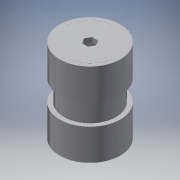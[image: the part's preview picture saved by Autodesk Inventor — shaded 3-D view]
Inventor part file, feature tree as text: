
AUTODESK INVENTOR PART (.ipt)
format: ipt  version: 2016 (Build 200138000, 138)  size: 152,064 bytes
history: native  units: in
note: dims shown in document units (in); Inventor stores cm internally (conversion verified against a paired STEP export)
features: extrude x6, sketch x6
ambient origin geometry x8: Origin, YZ Plane, XZ Plane, XY Plane, X Axis, Y Axis, Z Axis, Center Point
bodies: Body1 (feature_tree)
feature tree (12):
  extrude  "Extrusion5"  Depth=0.203in
  extrude  "Extrusion6"  Depth=2.5in
  extrude  "Extrusion7"  Depth=1.5in TaperAngle=0.0deg
  extrude  "Extrusion8"  Depth=1.5in TaperAngle=0.0deg
  extrude  "Extrusion9"  Depth=0.203in TaperAngle=0.0deg
  extrude  "Extrusion10"  Depth=0.5in TaperAngle=0.0deg
  sketch  "Sketch6"  dims[d16=2.5in d17=0.203in]
  sketch  "Sketch7"  dims[d18=2.5in d19=0.0in d20=2.5in]
  sketch  "Sketch8"  dims[d21=0.203in d22=1.5in d23=0.0in]
  sketch  "Sketch9"  dims[d24=0.203in d25=0.0in d26=1.5in d27=0.0in]
  sketch  "Sketch10"  dims[d28=2.4996in d29=0.203in d30=0.0in]
  sketch  "Sketch11"  dims[d31=0.5in d32=9.0in d33=0.0in]
